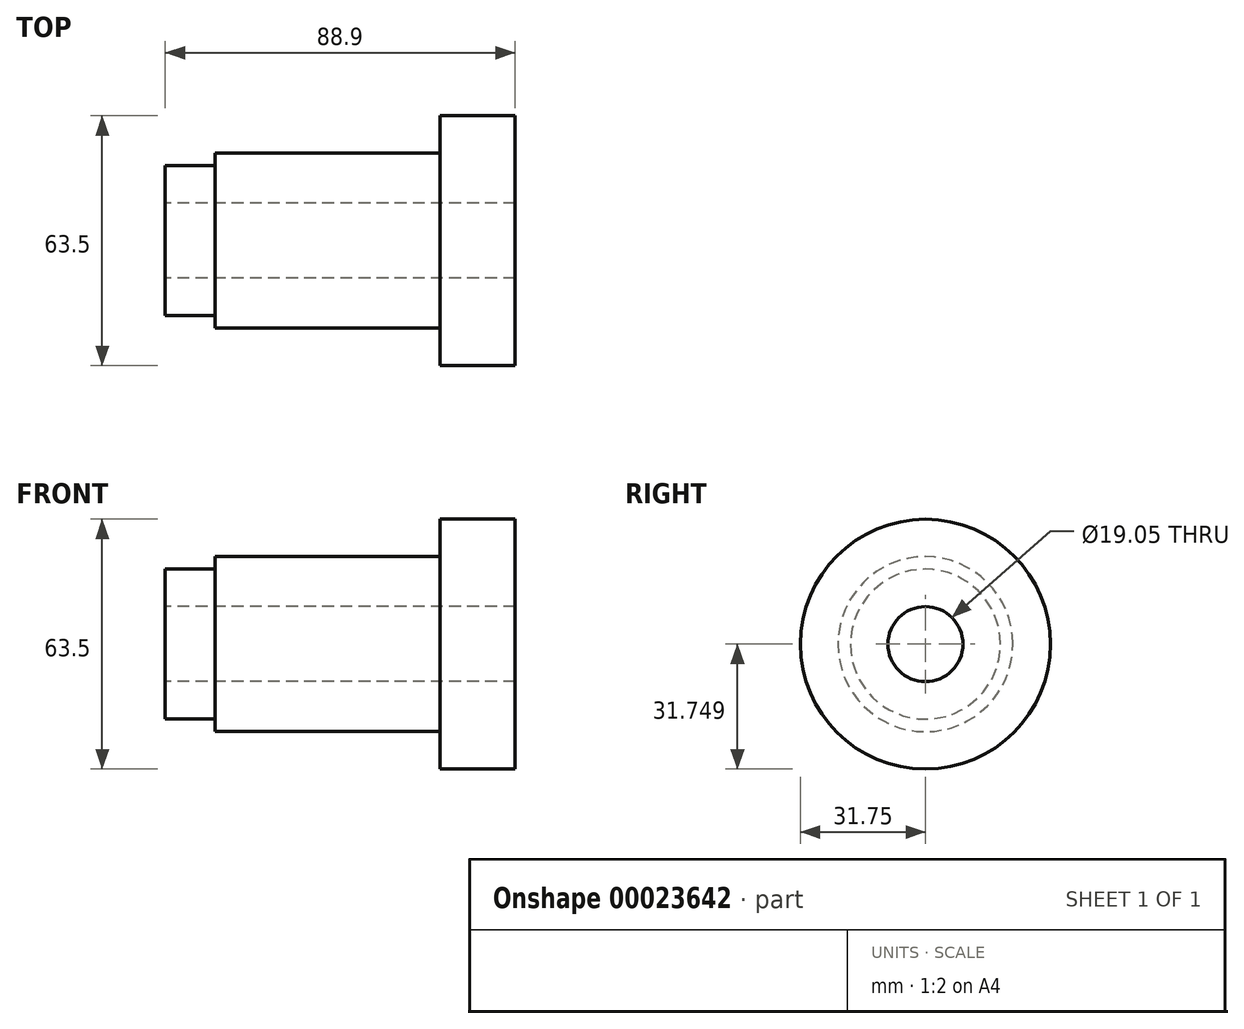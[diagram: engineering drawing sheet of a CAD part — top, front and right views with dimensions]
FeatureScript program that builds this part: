
annotation { "Feature Type Name" : "Feature", "Feature Type Description" : "" }
export const myFeature = defineFeature(function(context is Context, id is Id, definition is map)
    precondition{}
    {
        {
            var Q0;
            Q0=qCreatedBy(makeId("Front.planeOp"),FACE);
            var sketch = newSketch(context, id + "F0", { "sketchPlane" : qUnion([Q0])});
            skLineSegment(sketch, "E0", {"start": v(-117.52, -21.11) * mm, "end": v(104.03, -21.11) * mm, "construction": true});
            skLineSegment(sketch, "E1", {"start": v(-119.87, -11.59) * mm, "end": v(99.6, -11.59) * mm});
            skLineSegment(sketch, "E2.bottom", {"start": v(-62.72, -11.59) * mm, "end": v(-50.02, -11.59) * mm});
            skLineSegment(sketch, "E2.top", {"start": v(-62.72, -2.06) * mm, "end": v(-50.02, -2.06) * mm});
            skLineSegment(sketch, "E2.left", {"start": v(-62.72, -11.59) * mm, "end": v(-62.72, -2.06) * mm});
            skLineSegment(sketch, "E2.right", {"start": v(-50.02, -11.59) * mm, "end": v(-50.02, -2.06) * mm});
            skLineSegment(sketch, "E3.bottom", {"start": v(-50.02, -11.59) * mm, "end": v(7.13, -11.59) * mm});
            skLineSegment(sketch, "E3.top", {"start": v(-50.02, 1.11) * mm, "end": v(7.13, 1.11) * mm});
            skLineSegment(sketch, "E3.left", {"start": v(-50.02, -11.59) * mm, "end": v(-50.02, 1.11) * mm});
            skLineSegment(sketch, "E3.right", {"start": v(7.13, -11.59) * mm, "end": v(7.13, 1.11) * mm});
            skLineSegment(sketch, "E4.bottom", {"start": v(7.13, -11.59) * mm, "end": v(26.18, -11.59) * mm});
            skLineSegment(sketch, "E4.top", {"start": v(7.13, 10.64) * mm, "end": v(26.18, 10.64) * mm});
            skLineSegment(sketch, "E4.left", {"start": v(7.13, -11.59) * mm, "end": v(7.13, 10.64) * mm});
            skLineSegment(sketch, "E4.right", {"start": v(26.18, -11.59) * mm, "end": v(26.18, 10.64) * mm});
            skSolve(sketch);
        }
        {
            var Q0;
            Q0 = qSketchRegion(id + "F0", true);
            var Q1;
            Q1=sQuery(id+"F0.wireOp",EDGE,"E0");
            revolve(context, id + "F1", {"entities" : qUnion([Q0]), "axis" : qUnion([Q1]), "revolveType" : RevolveType.FULL});
        }
    });
